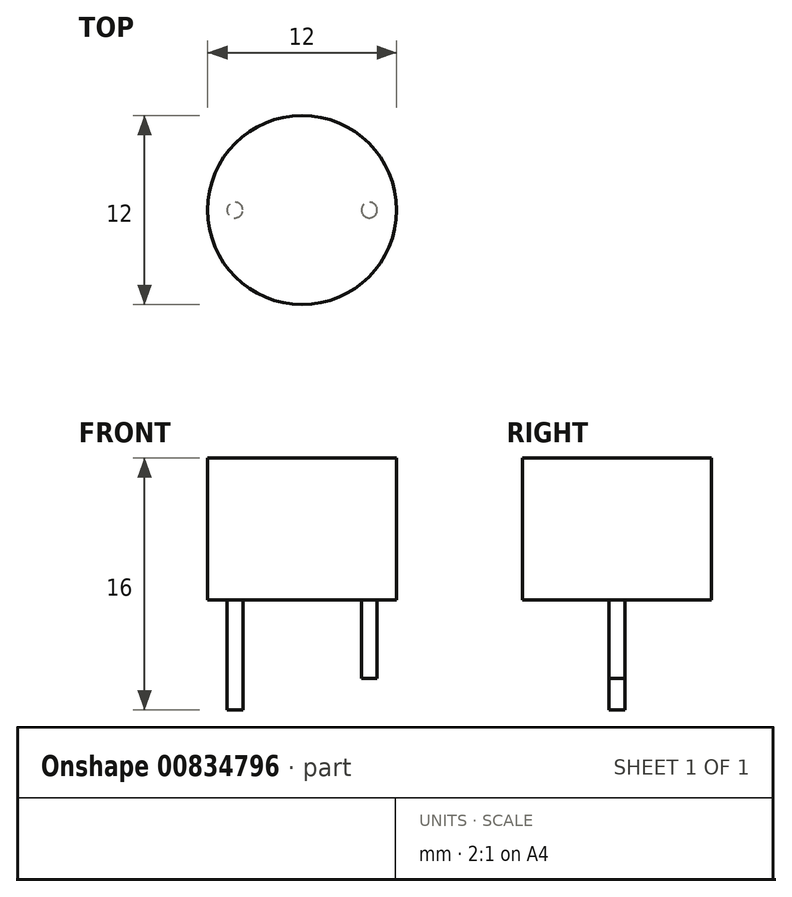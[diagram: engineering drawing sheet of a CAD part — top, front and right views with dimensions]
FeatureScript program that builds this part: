
annotation { "Feature Type Name" : "Feature", "Feature Type Description" : "" }
export const myFeature = defineFeature(function(context is Context, id is Id, definition is map)
    precondition{}
    {
        {
            var Q0;
            Q0=qCreatedBy(makeId("Top.planeOp"),FACE);
            var sketch = newSketch(context, id + "F0", { "sketchPlane" : qUnion([Q0])});
            skCircle(sketch, "E0", {"center": v(0, 0) * mm, "radius": 6 * mm});
            skSolve(sketch);
        }
        {
            var Q0;
            Q0 = qSketchRegion(id + "F0", true);
            extrude(context, id + "F1", {"entities" : qUnion([Q0]), "depth" : 9 * mm, "offsetDistance" : 25 * mm});
        }
        {
            var Q0;
            Q0=makeQuery(id+"F1.opExtrude","CAP_FACE",FACE,{"disambiguationData":[OSD([sQuery(id+"F0.wireOp",EDGE,"E0")])],"isStart":true});
            var sketch = newSketch(context, id + "F2", { "sketchPlane" : qUnion([Q0])});
            skCircle(sketch, "E1", {"center": v(4.27, 0) * mm, "radius": 0.5 * mm});
            skCircle(sketch, "E2", {"center": v(-4.27, 0) * mm, "radius": 0.5 * mm});
            skLineSegment(sketch, "E3", {"start": v(0, 0) * mm, "end": v(0, -3.42) * mm, "construction": true});
            skSolve(sketch);
        }
        {
            var Q0;
            Q0=makeQuery(id+"F2.imprint","IMPRINT",FACE,{"disambiguationData":[TD([[makeQuery(id+"F2.imprint","IMPRINT",EDGE,{"derivedFrom":sQuery(id+"F2.wireOp",EDGE,"E2")}),1.0]])]});
            extrude(context, id + "F3", {"entities" : qUnion([Q0]), "operationType" : NewBodyOperationType.ADD, "depth" : 7 * mm, "offsetDistance" : 25 * mm});
        }
        {
            var Q0;
            Q0=makeQuery(id+"F2.imprint","IMPRINT",FACE,{"disambiguationData":[TD([[makeQuery(id+"F2.imprint","IMPRINT",EDGE,{"derivedFrom":sQuery(id+"F2.wireOp",EDGE,"E1")}),1.0]])]});
            extrude(context, id + "F4", {"entities" : qUnion([Q0]), "operationType" : NewBodyOperationType.ADD, "depth" : 5 * mm, "offsetDistance" : 25 * mm});
        }
    });
